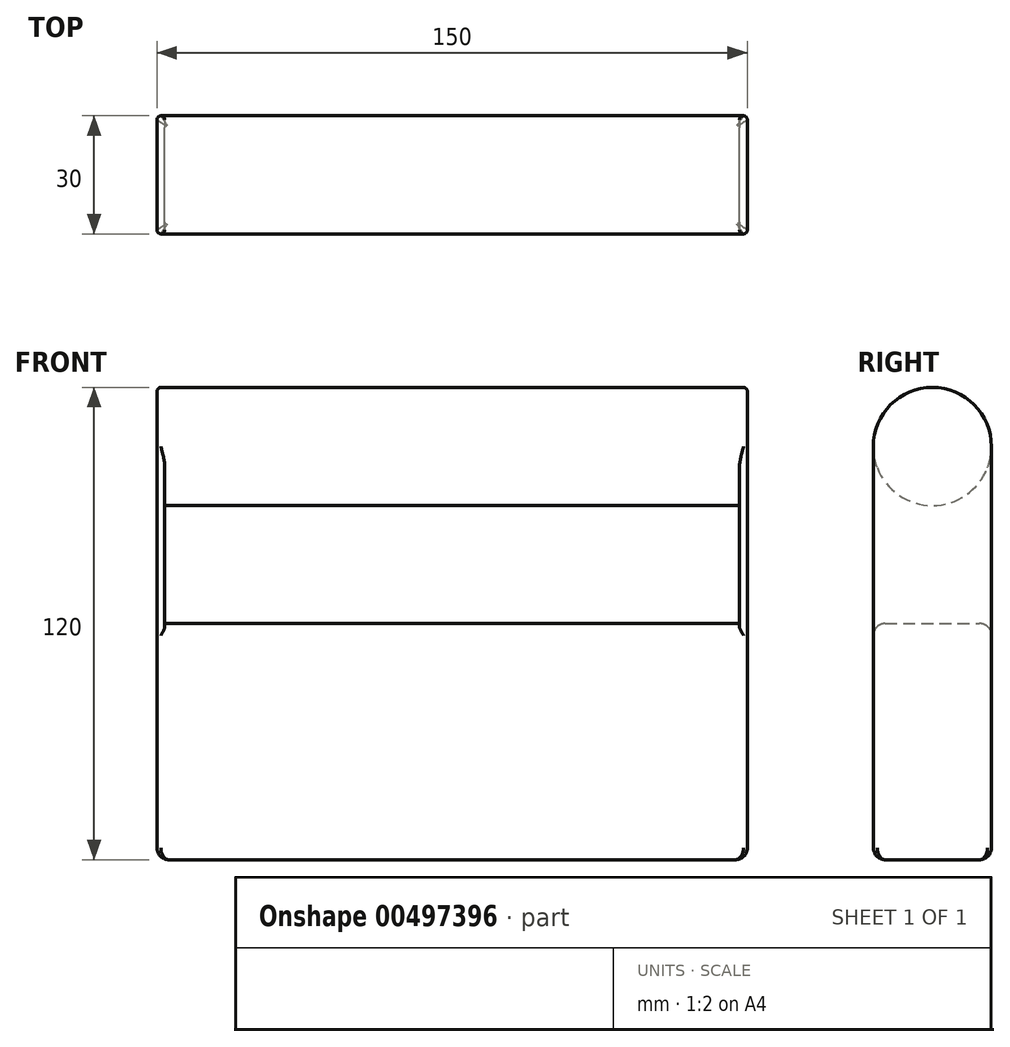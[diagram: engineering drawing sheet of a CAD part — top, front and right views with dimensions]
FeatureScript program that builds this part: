
annotation { "Feature Type Name" : "Feature", "Feature Type Description" : "" }
export const myFeature = defineFeature(function(context is Context, id is Id, definition is map)
    precondition{}
    {
        {
            var Q0;
            Q0=qCreatedBy(makeId("Front.planeOp"),FACE);
            var sketch = newSketch(context, id + "F0", { "sketchPlane" : qUnion([Q0])});
            skLineSegment(sketch, "E0.bottom", {"start": v(-75, 30) * mm, "end": v(75, 30) * mm});
            skLineSegment(sketch, "E0.top", {"start": v(-75, -30) * mm, "end": v(75, -30) * mm});
            skLineSegment(sketch, "E0.left", {"start": v(-75, 30) * mm, "end": v(-75, -30) * mm});
            skLineSegment(sketch, "E0.right", {"start": v(75, 30) * mm, "end": v(75, -30) * mm});
            skPoint(sketch, "E0.middle", {"position": v(0, 0) * mm});
            skLineSegment(sketch, "E1", {"start": v(-75, 30) * mm, "end": v(-75, 90) * mm});
            skLineSegment(sketch, "E2", {"start": v(75, 30) * mm, "end": v(75, 90) * mm});
            skLineSegment(sketch, "E3", {"start": v(75, 90) * mm, "end": v(-75, 90) * mm});
            skLineSegment(sketch, "E4", {"start": v(-75, 60) * mm, "end": v(75, 60) * mm});
            skLineSegment(sketch, "E5", {"start": v(-73, 60) * mm, "end": v(-73, 30) * mm});
            skLineSegment(sketch, "E6", {"start": v(73, 60) * mm, "end": v(73, 30) * mm});
            skSolve(sketch);
        }
        {
            var Q0;
            Q0 = qSketchRegion(id + "F0", true);
            extrude(context, id + "F1", {"entities" : qUnion([Q0]), "endBound" : BoundingType.SYMMETRIC, "depth" : 30 * mm});
        }
        {
            var Q0;
            Q0=makeQuery(id+"F1.opExtrude","CAP_EDGE",EDGE,{"disambiguationData":[OSD([sQuery(id+"F0.wireOp",EDGE,"E3")])],"isStart":false});
            var Q1;
            Q1=makeQuery(id+"F1.opExtrude","CAP_EDGE",EDGE,{"disambiguationData":[OSD([sQuery(id+"F0.wireOp",EDGE,"E4")])],"isStart":false});
            var Q2;
            Q2=makeQuery(id+"F1.opExtrude","CAP_EDGE",EDGE,{"disambiguationData":[OSD([sQuery(id+"F0.wireOp",EDGE,"E3")])],"isStart":true});
            var Q3;
            Q3=makeQuery(id+"F1.opExtrude","CAP_EDGE",EDGE,{"disambiguationData":[OSD([sQuery(id+"F0.wireOp",EDGE,"E4")])],"isStart":true});
            fillet(context, id + "F2", {"entities" : qUnion([Q0, Q1, Q2, Q3]), "radius" : 15 * mm, "tangentPropagation" : true, "allowEdgeOverflow" : false});
        }
        {
            var Q0;
            Q0=makeQuery(id+"F1.opExtrude","CAP_EDGE",EDGE,{"disambiguationData":[OSD([sQuery(id+"F0.wireOp",EDGE,"E0.bottom")])],"isStart":false});
            var Q1;
            Q1=makeQuery(id+"F1.opExtrude","CAP_EDGE",EDGE,{"disambiguationData":[OSD([sQuery(id+"F0.wireOp",EDGE,"E0.bottom")])],"isStart":true});
            var Q2;
            Q2=makeQuery(id+"F1.opExtrude","CAP_EDGE",EDGE,{"disambiguationData":[OSD([sQuery(id+"F0.wireOp",EDGE,"E0.top")])],"isStart":false});
            var Q3;
            Q3=makeQuery(id+"F1.opExtrude","SWEPT_EDGE",EDGE,{"disambiguationData":[OSD([sQuery(id+"F0.wireOp",EDGE,"E0.top"),sQuery(id+"F0.wireOp",EDGE,"E0.right")])]});
            var Q4;
            Q4=makeQuery(id+"F1.opExtrude","CAP_EDGE",EDGE,{"disambiguationData":[OSD([sQuery(id+"F0.wireOp",EDGE,"E0.top")])],"isStart":true});
            var Q5;
            Q5=makeQuery(id+"F1.opExtrude","SWEPT_EDGE",EDGE,{"disambiguationData":[OSD([sQuery(id+"F0.wireOp",EDGE,"E0.top"),sQuery(id+"F0.wireOp",EDGE,"E0.left")])]});
            fillet(context, id + "F3", {"entities" : qUnion([Q0, Q1, Q2, Q3, Q4, Q5]), "radius" : 3 * mm, "tangentPropagation" : true, "allowEdgeOverflow" : false});
        }
        {
            var Q0;
            Q0=makeQuery(id+"F1.opExtrude","CAP_EDGE",EDGE,{"disambiguationData":[OSD([sQuery(id+"F0.wireOp",EDGE,"E0.right"),sQuery(id+"F0.wireOp",EDGE,"E2")])],"isStart":false});
            var Q1;
            Q1=makeQuery(id+"F1.opExtrude","CAP_EDGE",EDGE,{"disambiguationData":[OSD([sQuery(id+"F0.wireOp",EDGE,"E0.right"),sQuery(id+"F0.wireOp",EDGE,"E2")])],"isStart":true});
            var Q2;
            Q2=makeQuery(id+"F1.opExtrude","CAP_EDGE",EDGE,{"disambiguationData":[OSD([sQuery(id+"F0.wireOp",EDGE,"E0.left"),sQuery(id+"F0.wireOp",EDGE,"E1")])],"isStart":false});
            var Q3;
            Q3=makeQuery(id+"F1.opExtrude","CAP_EDGE",EDGE,{"disambiguationData":[OSD([sQuery(id+"F0.wireOp",EDGE,"E0.left"),sQuery(id+"F0.wireOp",EDGE,"E1")])],"isStart":true});
            var Q4;
            Q4=makeQuery(id+"F1.opExtrude","CAP_EDGE",EDGE,{"disambiguationData":[OSD([sQuery(id+"F0.wireOp",EDGE,"E5")])],"isStart":false});
            var Q5;
            Q5=makeQuery(id+"F1.opExtrude","CAP_EDGE",EDGE,{"disambiguationData":[OSD([sQuery(id+"F0.wireOp",EDGE,"E5")])],"isStart":true});
            var Q6;
            Q6=makeQuery(id+"F1.opExtrude","CAP_EDGE",EDGE,{"disambiguationData":[OSD([sQuery(id+"F0.wireOp",EDGE,"E6")])],"isStart":false});
            var Q7;
            Q7=makeQuery(id+"F1.opExtrude","CAP_EDGE",EDGE,{"disambiguationData":[OSD([sQuery(id+"F0.wireOp",EDGE,"E6")])],"isStart":true});
            fillet(context, id + "F4", {"entities" : qUnion([Q0, Q1, Q2, Q3, Q4, Q5, Q6, Q7]), "radius" : 1 * mm, "tangentPropagation" : true, "allowEdgeOverflow" : false});
        }
    });
